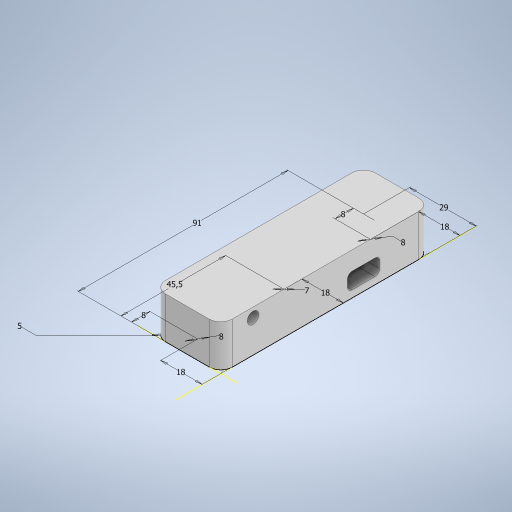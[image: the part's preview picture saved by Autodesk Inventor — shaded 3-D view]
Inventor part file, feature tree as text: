
AUTODESK INVENTOR PART (.ipt)
format: ipt  version: 2024.3 (Build 283343000, 343)  size: 276,992 bytes
history: native  units: in
note: dims shown in document units (in); Inventor stores cm internally (conversion verified against a paired STEP export)
features: extrude x3, sketch x2
ambient origin geometry x8: Origin, YZ Plane, XZ Plane, XY Plane, X Axis, Y Axis, Z Axis, Center Point
bodies: Solid1 (feature_tree)
feature tree (5):
  sketch  "Sketch1"  dims[d0=1.1417in d1=3.5827in]
  extrude  "Extrusion1"  Depth=3.5827in
  sketch  "Sketch2"  dims[d2=0.1969in d3=0.315in d4=0.2756in d5=0.315in d6=0.7087in d7=1.7913in d8=0.7087in d9=0.315in d10=0.315in d11=0.7087in d12=0.7087in d13=0.0in d14=0.1969in d15=0.5512in d16=0.5512in d17=0.5512in d18=0.2756in d19=0.0787in d20=2.1654in d21=0.1181in d22=0.0787in d23=0.0in d24=0.315in d25=0.0in]
  extrude  "Extrusion2"  Depth=0.315in
  extrude  "Extrusion3"  Depth=0.2756in
